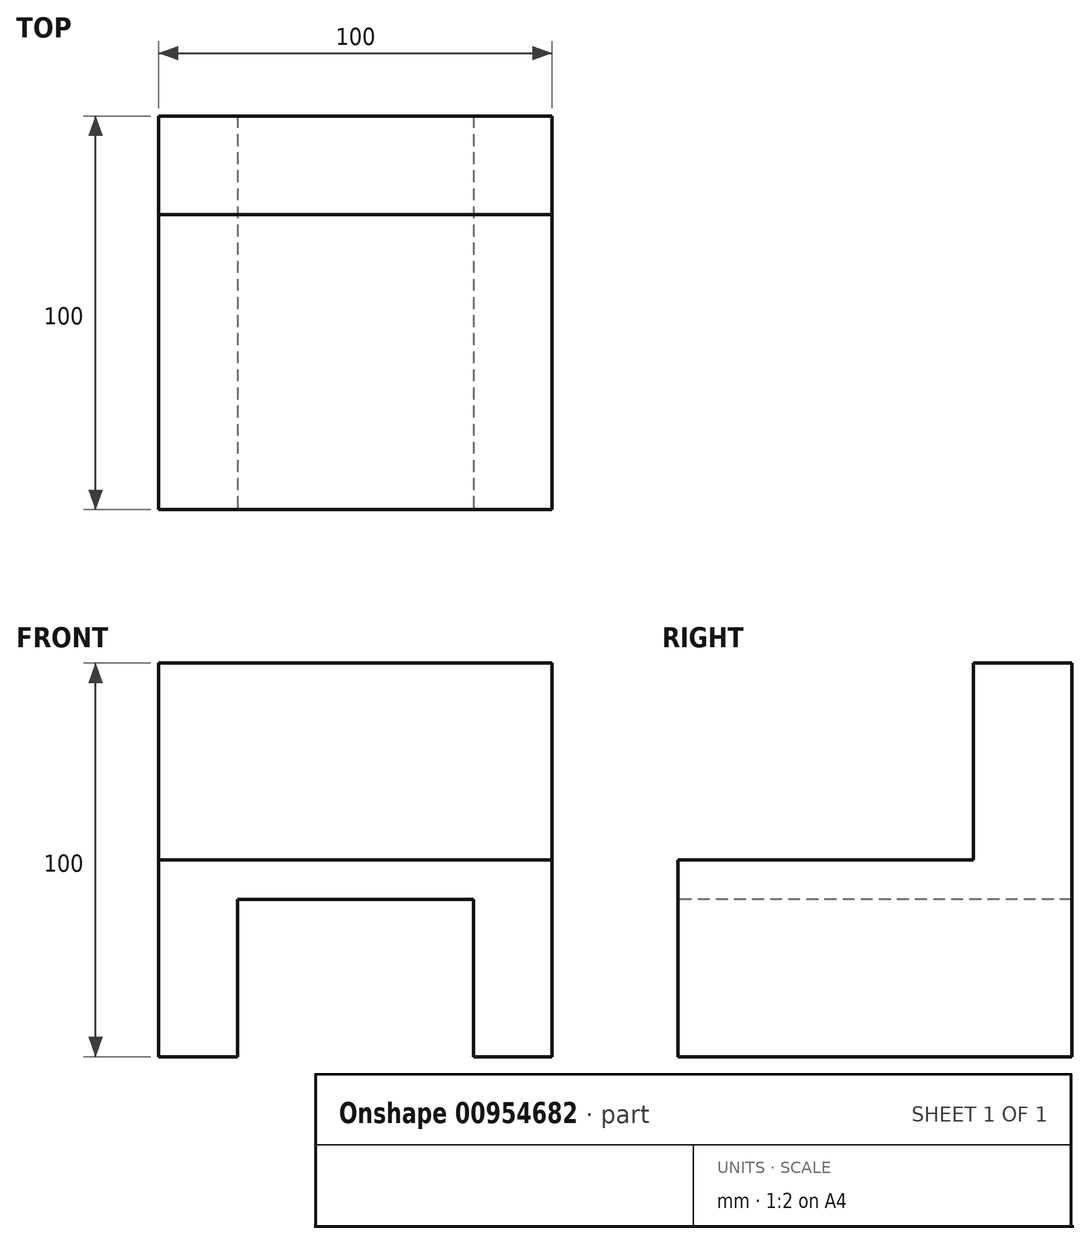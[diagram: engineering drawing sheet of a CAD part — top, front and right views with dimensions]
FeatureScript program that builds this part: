
annotation { "Feature Type Name" : "Feature", "Feature Type Description" : "" }
export const myFeature = defineFeature(function(context is Context, id is Id, definition is map)
    precondition{}
    {
        {
            var Q0;
            Q0=qCreatedBy(makeId("Top.planeOp"),FACE);
            var sketch = newSketch(context, id + "F0", { "sketchPlane" : qUnion([Q0])});
            skLineSegment(sketch, "E0.bottom", {"start": v(50, 50) * mm, "end": v(-50, 50) * mm});
            skLineSegment(sketch, "E0.top", {"start": v(50, -50) * mm, "end": v(-50, -50) * mm});
            skLineSegment(sketch, "E0.left", {"start": v(50, 50) * mm, "end": v(50, -50) * mm});
            skLineSegment(sketch, "E0.right", {"start": v(-50, 50) * mm, "end": v(-50, -50) * mm});
            skPoint(sketch, "E0.middle", {"position": v(0, 0) * mm});
            skSolve(sketch);
        }
        {
            var Q0;
            Q0=makeQuery(id+"F0.imprint","IMPRINT",FACE,{"disambiguationData":[TD([[makeQuery(id+"F0.imprint","IMPRINT",EDGE,{"derivedFrom":sQuery(id+"F0.wireOp",EDGE,"E0.bottom")}),1.0]])]});
            extrude(context, id + "F1", {"entities" : qUnion([Q0]), "depth" : 100 * mm, "offsetDistance" : 25 * mm});
        }
        {
            var Q0;
            Q0=makeQuery(id+"F1.opExtrude","CAP_FACE",FACE,{"disambiguationData":[OSD([sQuery(id+"F0.wireOp",EDGE,"E0.bottom"),sQuery(id+"F0.wireOp",EDGE,"E0.top"),sQuery(id+"F0.wireOp",EDGE,"E0.left"),sQuery(id+"F0.wireOp",EDGE,"E0.right")])],"isStart":false});
            var sketch = newSketch(context, id + "F2", { "sketchPlane" : qUnion([Q0])});
            skLineSegment(sketch, "E1.bottom", {"start": v(-50, 0) * mm, "end": v(50, 0) * mm});
            skLineSegment(sketch, "E1.top", {"start": v(-50, -50) * mm, "end": v(50, -50) * mm});
            skLineSegment(sketch, "E1.left", {"start": v(-50, 0) * mm, "end": v(-50, -50) * mm});
            skLineSegment(sketch, "E1.right", {"start": v(50, 0) * mm, "end": v(50, -50) * mm});
            skSolve(sketch);
        }
        {
            var Q0;
            Q0 = qSketchRegion(id + "F2", true);
            extrude(context, id + "F3", {"entities" : qUnion([Q0]), "operationType" : NewBodyOperationType.REMOVE, "oppositeDirection" : true, "depth" : 50 * mm, "offsetDistance" : 25 * mm});
        }
        {
            var Q0;
            Q0=makeQuery(id+"F3.boolean.opBoolean","COPY",FACE,{"derivedFrom":makeQuery(id+"F3.opExtrude","SWEPT_FACE",FACE,{"disambiguationData":[OSD([sQuery(id+"F2.wireOp",EDGE,"E1.bottom")])]})});
            extrude(context, id + "F4", {"entities" : qUnion([Q0]), "operationType" : NewBodyOperationType.REMOVE, "oppositeDirection" : true, "depth" : 25 * mm, "offsetDistance" : 25 * mm});
        }
        {
            var Q0;
            Q0=makeQuery(id+"F1.opExtrude","SWEPT_FACE",FACE,{"disambiguationData":[OSD([sQuery(id+"F0.wireOp",EDGE,"E0.top")])]});
            var sketch = newSketch(context, id + "F5", { "sketchPlane" : qUnion([Q0])});
            skLineSegment(sketch, "E2.bottom", {"start": v(-30, 0) * mm, "end": v(30, 0) * mm});
            skLineSegment(sketch, "E2.top", {"start": v(-30, 40) * mm, "end": v(30, 40) * mm});
            skLineSegment(sketch, "E2.left", {"start": v(-30, 0) * mm, "end": v(-30, 40) * mm});
            skLineSegment(sketch, "E2.right", {"start": v(30, 0) * mm, "end": v(30, 40) * mm});
            skSolve(sketch);
        }
        {
            var Q0;
            Q0 = qSketchRegion(id + "F5", true);
            extrude(context, id + "F6", {"entities" : qUnion([Q0]), "operationType" : NewBodyOperationType.REMOVE, "oppositeDirection" : true, "depth" : 100 * mm, "offsetDistance" : 25 * mm});
        }
    });
